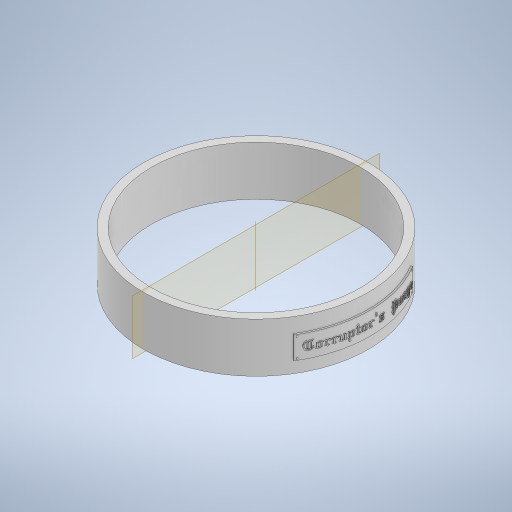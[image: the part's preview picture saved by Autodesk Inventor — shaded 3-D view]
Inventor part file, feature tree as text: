
AUTODESK INVENTOR PART (.ipt)
format: ipt  version: 2023 (Build 270158000, 158)  size: 6,275,584 bytes
history: native  units: in
note: dims shown in document units (in); Inventor stores cm internally (conversion verified against a paired STEP export)
features: emboss x3, pattern_circular x3, other x2, extrude x1, plane x1, fillet x1, sketch x1
ambient origin geometry x8: Origin, YZ Plane, XZ Plane, XY Plane, X Axis, Y Axis, Z Axis, Center Point
bodies: Solid1 (feature_tree)
feature tree (12):
  extrude  "Extrusion1"  Depth=0.3937in
  plane  "Work Plane1"
  other  "Text"
  emboss  "Emboss4"
  emboss  "Emboss5"
  emboss  "Emboss6"
  fillet  "Rivots"  Radius=0.8661in
  pattern_circular  "Circular Pattern1"  Count=6  [1 undecoded]
  pattern_circular  "Circular Pattern2"  [2 undecoded]
  pattern_circular  "Circular Pattern3"  [2 undecoded]
  sketch  "Sketch1"  dims[d0=3.937in d1=3.6614in d2=0.8661in d3=0.0in d4=2.3622in d6=0.4546in d10=0.0in d11=0.3937in d12=2.1654in d19=0.0in d20=0.0in d21=0.0295in d22=0.0in d23=0.0197in d24=0.0in d25=0.0295in d26=0.0295in d27=0.0295in d28=0.0157in d29=0.0in d30=0.0138in d31=0.7874in d32=360.0deg d34=0.7874in d35=360.0deg d37=0.7874in d38=360.0deg d33=0.0in]
  other  "NamePlate"
note: 5 required parameter values undecoded (feature->parameter linkage not recoverable at this tier; creation-order binding heuristic only, values carry confidence <= 0.55)
